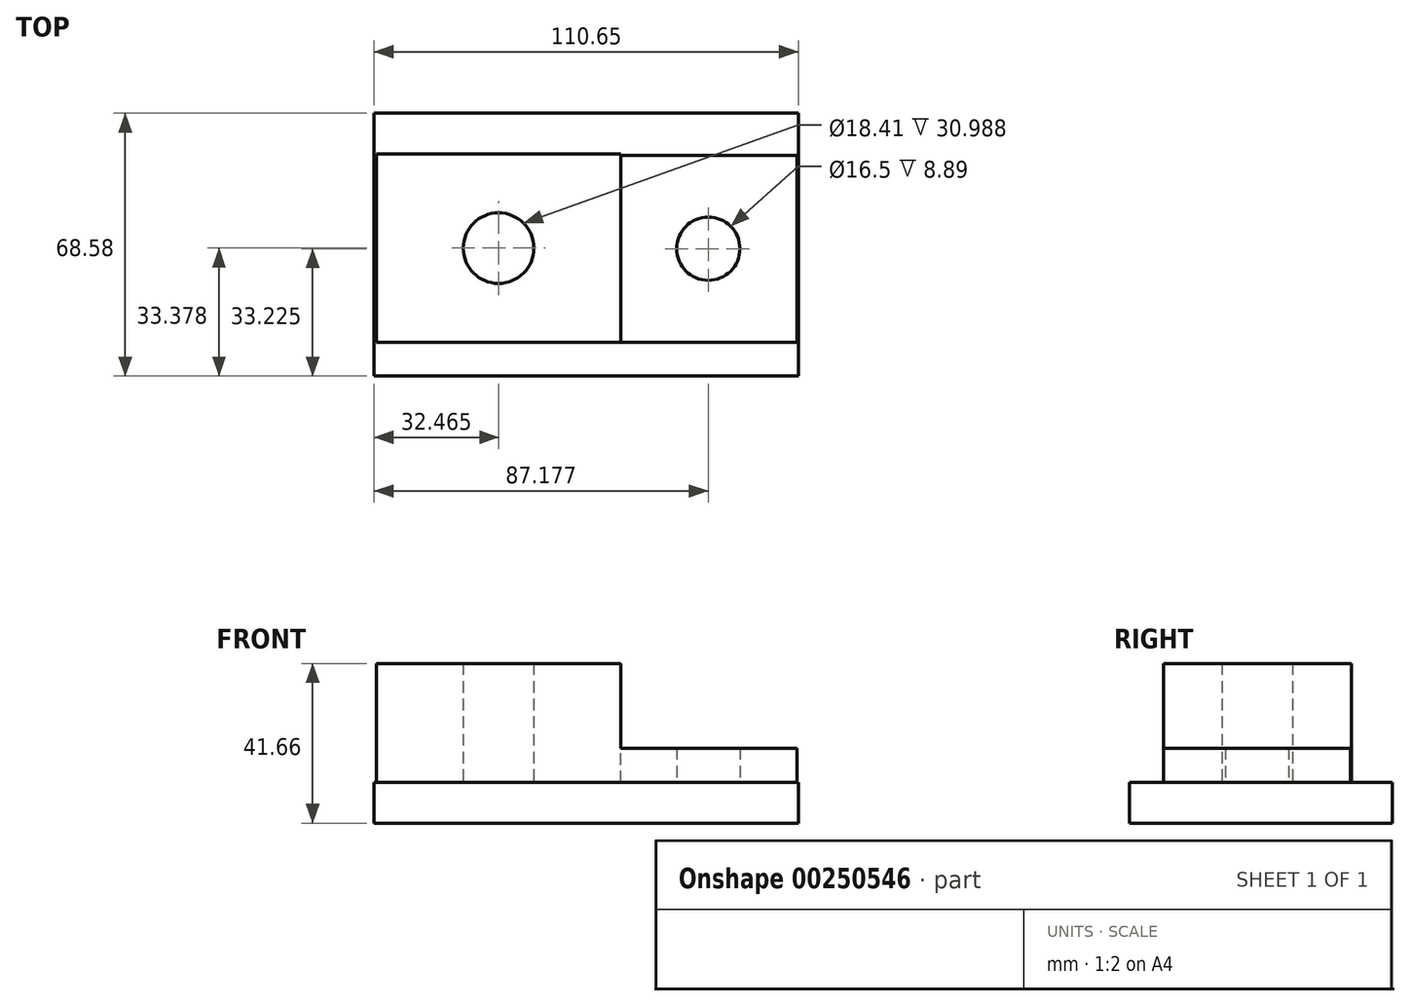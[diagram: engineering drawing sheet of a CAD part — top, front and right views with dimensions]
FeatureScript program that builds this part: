
annotation { "Feature Type Name" : "Feature", "Feature Type Description" : "" }
export const myFeature = defineFeature(function(context is Context, id is Id, definition is map)
    precondition{}
    {
        {
            var Q0;
            Q0=qCreatedBy(makeId("Top.planeOp"),FACE);
            var sketch = newSketch(context, id + "F0", { "sketchPlane" : qUnion([Q0])});
            skLineSegment(sketch, "E0.bottom", {"start": v(-66.45, 35.81) * mm, "end": v(-2.74, 35.81) * mm});
            skLineSegment(sketch, "E0.top", {"start": v(-66.45, -13.26) * mm, "end": v(-2.74, -13.26) * mm});
            skLineSegment(sketch, "E0.left", {"start": v(-66.45, 35.81) * mm, "end": v(-66.45, -13.26) * mm});
            skLineSegment(sketch, "E0.right", {"start": v(-2.74, 35.81) * mm, "end": v(-2.74, -13.26) * mm});
            skCircle(sketch, "E1", {"center": v(-34.6, 11.28) * mm, "radius": 9.2 * mm});
            skPoint(sketch, "E1.centerSnap0", {"position": v(-66.45, 11.28) * mm});
            skPoint(sketch, "E1.centerSnap1", {"position": v(-34.6, 35.81) * mm});
            skSolve(sketch);
        }
        {
            var Q0;
            Q0 = qSketchRegion(id + "F0", true);
            extrude(context, id + "F1", {"entities" : qUnion([Q0]), "depth" : 30.99 * mm});
        }
        {
            var Q0;
            Q0=qCreatedBy(makeId("Top.planeOp"),FACE);
            var sketch = newSketch(context, id + "F2", { "sketchPlane" : qUnion([Q0])});
            skLineSegment(sketch, "E2.bottom", {"start": v(-3.05, 35.5) * mm, "end": v(43.28, 35.5) * mm});
            skLineSegment(sketch, "E2.top", {"start": v(-3.05, -13.26) * mm, "end": v(43.28, -13.26) * mm});
            skLineSegment(sketch, "E2.left", {"start": v(-3.05, 35.5) * mm, "end": v(-3.05, -13.26) * mm});
            skLineSegment(sketch, "E2.right", {"start": v(43.28, 35.5) * mm, "end": v(43.28, -13.26) * mm});
            skCircle(sketch, "E3", {"center": v(20.12, 11.13) * mm, "radius": 8.25 * mm});
            skPoint(sketch, "E3.centerSnap0", {"position": v(-3.05, 11.13) * mm});
            skPoint(sketch, "E3.centerSnap1", {"position": v(20.12, 35.5) * mm});
            skSolve(sketch);
        }
        {
            var Q0;
            Q0 = qSketchRegion(id + "F2", true);
            extrude(context, id + "F3", {"entities" : qUnion([Q0]), "operationType" : NewBodyOperationType.ADD, "depth" : 8.9 * mm});
        }
        {
            var Q0;
            Q0=makeQuery(id+"F3.boolean.opBoolean","MERGE",FACE,{"derivedFrom":[makeQuery(id+"F1.opExtrude","CAP_FACE",FACE,{"disambiguationData":[OSD([sQuery(id+"F0.wireOp",EDGE,"E0.bottom"),sQuery(id+"F0.wireOp",EDGE,"E0.top"),sQuery(id+"F0.wireOp",EDGE,"E0.left"),sQuery(id+"F0.wireOp",EDGE,"E0.right"),sQuery(id+"F0.wireOp",EDGE,"E1")])],"isStart":true}),makeQuery(id+"F3.opExtrude","CAP_FACE",FACE,{"disambiguationData":[OSD([sQuery(id+"F2.wireOp",EDGE,"E2.bottom"),sQuery(id+"F2.wireOp",EDGE,"E2.top"),sQuery(id+"F2.wireOp",EDGE,"E2.left"),sQuery(id+"F2.wireOp",EDGE,"E2.right"),sQuery(id+"F2.wireOp",EDGE,"E3")])],"isStart":true})]});
            var sketch = newSketch(context, id + "F4", { "sketchPlane" : qUnion([Q0])});
            skLineSegment(sketch, "E4.bottom", {"start": v(-67.06, 22.1) * mm, "end": v(43.59, 22.1) * mm});
            skLineSegment(sketch, "E4.top", {"start": v(-67.06, -46.48) * mm, "end": v(43.59, -46.48) * mm});
            skLineSegment(sketch, "E4.left", {"start": v(-67.06, 22.1) * mm, "end": v(-67.06, -46.48) * mm});
            skLineSegment(sketch, "E4.right", {"start": v(43.59, 22.1) * mm, "end": v(43.59, -46.48) * mm});
            skSolve(sketch);
        }
        {
            var Q0;
            Q0 = qSketchRegion(id + "F4", true);
            extrude(context, id + "F5", {"entities" : qUnion([Q0]), "operationType" : NewBodyOperationType.ADD, "depth" : 10.67 * mm});
        }
    });
